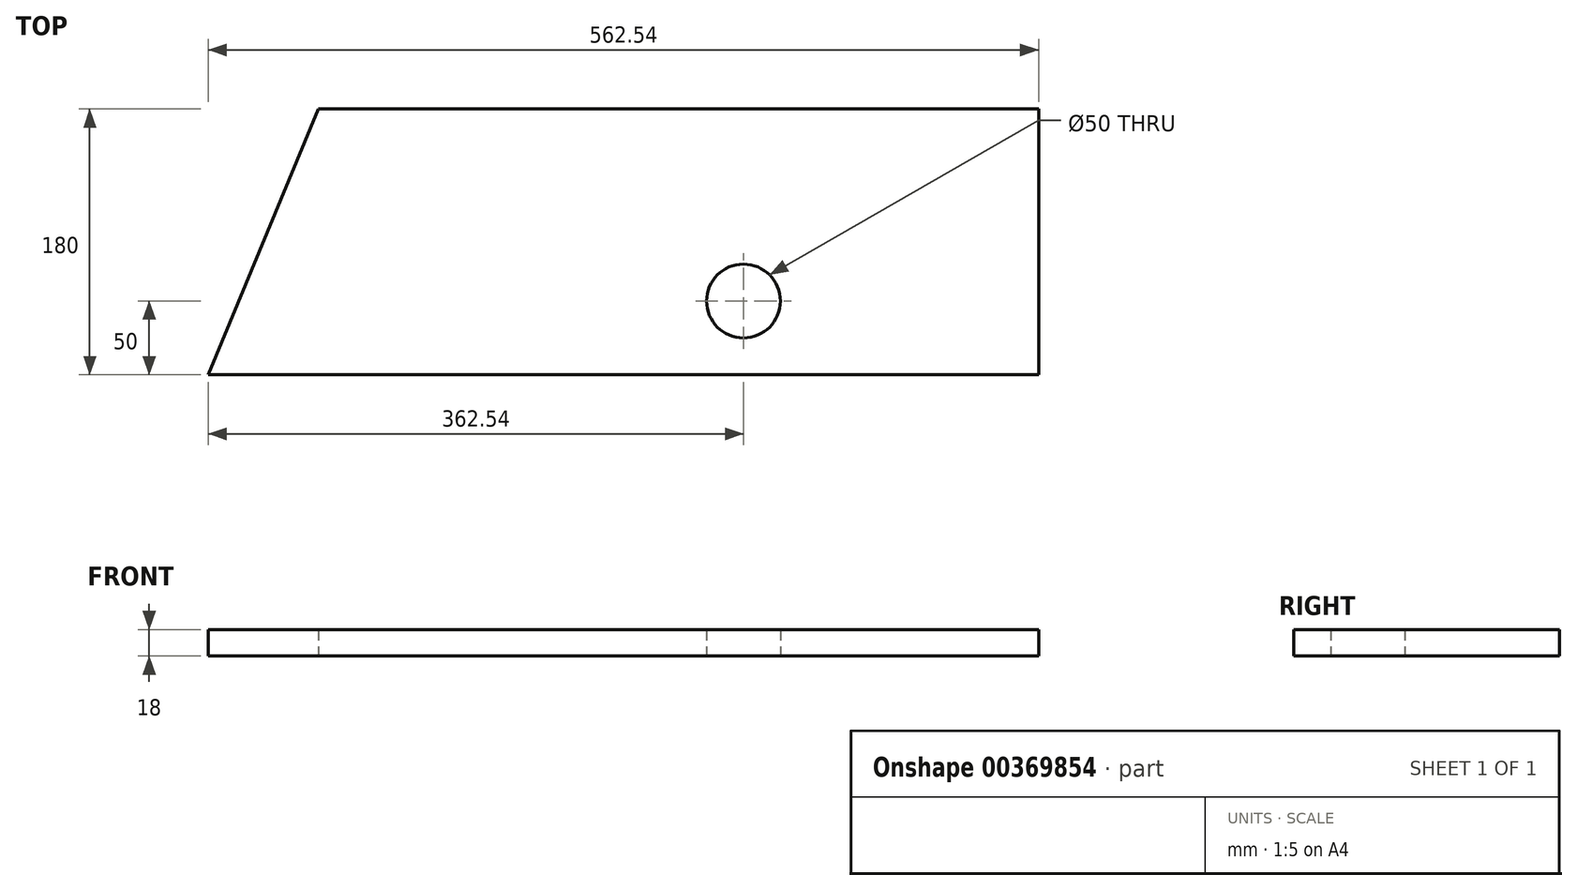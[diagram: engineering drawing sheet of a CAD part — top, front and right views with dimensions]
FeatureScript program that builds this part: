
annotation { "Feature Type Name" : "Feature", "Feature Type Description" : "" }
export const myFeature = defineFeature(function(context is Context, id is Id, definition is map)
    precondition{}
    {
        {
            var Q0;
            Q0=qCreatedBy(makeId("Top.planeOp"),FACE);
            var sketch = newSketch(context, id + "F0", { "sketchPlane" : qUnion([Q0])});
            skLineSegment(sketch, "E0", {"start": v(0, 0) * mm, "end": v(-562.54, 0) * mm});
            skLineSegment(sketch, "E1", {"start": v(-562.54, 0) * mm, "end": v(-1407.21, 844.67) * mm, "construction": true});
            skLineSegment(sketch, "E2", {"start": v(-1407.21, 844.67) * mm, "end": v(-1152.66, 844.67) * mm, "construction": true});
            skLineSegment(sketch, "E3", {"start": v(-1152.66, 844.67) * mm, "end": v(-487.99, 180) * mm, "construction": true});
            skLineSegment(sketch, "E4", {"start": v(-487.99, 180) * mm, "end": v(0, 180) * mm});
            skLineSegment(sketch, "E5", {"start": v(0, 180) * mm, "end": v(0, 0) * mm});
            skLineSegment(sketch, "E6", {"start": v(0, 1382) * mm, "end": v(0, 180) * mm, "construction": true});
            skCircle(sketch, "E7", {"center": v(-200, 50) * mm, "radius": 25 * mm});
            skLineSegment(sketch, "E8", {"start": v(0, -18) * mm, "end": v(-570, -18) * mm, "construction": true});
            skLineSegment(sketch, "E9", {"start": v(-570, -18) * mm, "end": v(-1432.67, 844.67) * mm, "construction": true});
            skLineSegment(sketch, "E10", {"start": v(-1170.66, 862.67) * mm, "end": v(-1432.67, 862.67) * mm, "construction": true});
            skLineSegment(sketch, "E11", {"start": v(-1432.67, 862.67) * mm, "end": v(-1432.67, 844.67) * mm});
            skLineSegment(sketch, "E12", {"start": v(-487.99, 180) * mm, "end": v(-562.54, 0) * mm});
            skSolve(sketch);
        }
        {
            var Q0;
            Q0=makeQuery(id+"F0.imprint","IMPRINT",FACE,{"disambiguationData":[TD([[makeQuery(id+"F0.imprint","IMPRINT",EDGE,{"derivedFrom":sQuery(id+"F0.wireOp",EDGE,"E0")}),-1.0]])]});
            extrude(context, id + "F1", {"entities" : qUnion([Q0]), "depth" : 18 * mm});
        }
    });
